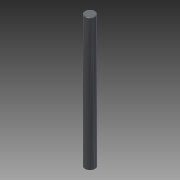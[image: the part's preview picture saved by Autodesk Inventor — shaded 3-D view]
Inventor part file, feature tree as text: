
AUTODESK INVENTOR PART (.ipt)
format: ipt  version: 2012 SP1 (Build 160190100, 190)  size: 73,216 bytes
history: native  units: mm
features: extrude x1, chamfer x1, sketch x1
ambient origin geometry x8: Origin, YZ Plane, XZ Plane, XY Plane, X Axis, Y Axis, Z Axis, Center Point
bodies: Solid1 (feature_tree)
feature tree (3):
  extrude  "Extrusion1"  Depth=130.0mm TaperAngle=0.0deg
  chamfer  "Chamfer1"  Distance=0.5mm Angle=45.0deg
  sketch  "Sketch1"  dims[d0=10.0mm d1=130.0mm d2=0.0mm d3=0.5mm d4=2.0mm d5=45.0deg]
